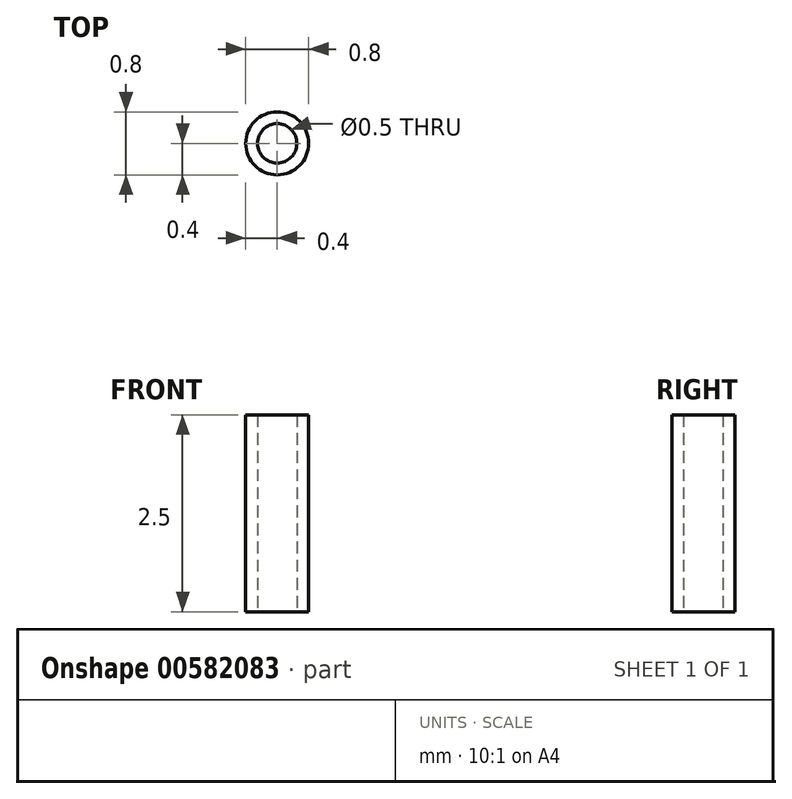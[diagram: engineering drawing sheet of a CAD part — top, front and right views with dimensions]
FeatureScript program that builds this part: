
annotation { "Feature Type Name" : "Feature", "Feature Type Description" : "" }
export const myFeature = defineFeature(function(context is Context, id is Id, definition is map)
    precondition{}
    {
        {
            var Q0;
            Q0=qCreatedBy(makeId("Top.planeOp"),FACE);
            var sketch = newSketch(context, id + "F0", { "sketchPlane" : qUnion([Q0])});
            skCircle(sketch, "E0", {"center": v(0, 0) * mm, "radius": 0.25 * mm});
            skCircle(sketch, "E1", {"center": v(0, 0) * mm, "radius": 0.4 * mm});
            skSolve(sketch);
        }
        {
            var Q0;
            Q0=makeQuery(id+"F0.imprint","IMPRINT",FACE,{"disambiguationData":[TD([[makeQuery(id+"F0.imprint","IMPRINT",EDGE,{"derivedFrom":sQuery(id+"F0.wireOp",EDGE,"E0")}),-1.0]])]});
            extrude(context, id + "F1", {"entities" : qUnion([Q0]), "depth" : 2.5 * mm, "offsetDistance" : 25 * mm});
        }
    });
